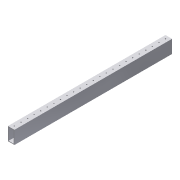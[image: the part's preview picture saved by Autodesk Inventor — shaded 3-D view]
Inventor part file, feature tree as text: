
AUTODESK INVENTOR PART (.ipt)
format: ipt  version: 2015 (Build 190159000, 159)  size: 127,488 bytes
history: native  units: in
note: dims shown in document units (in); Inventor stores cm internally (conversion verified against a paired STEP export)
features: sketch x2, extrude x1, hole x1, pattern_linear x1
ambient origin geometry x8: Origin, YZ Plane, XZ Plane, XY Plane, X Axis, Y Axis, Z Axis, Center Point
bodies: Solid1 (feature_tree)
feature tree (5):
  extrude  "Extrusion1"  Depth=2.0in
  hole  "Hole1"  [1 undecoded]
  pattern_linear  "Rectangular Pattern1"  Spacing1=0.5in  [1 undecoded]
  sketch  "Sketch1"  dims[d0=1.0in d1=2.0in]
  sketch  "Sketch2"  dims[d2=0.1in d4=0.0in d6=0.5in d7=0.164in d8=0.75in d9=0.375in d10=0.25in d11=0.5635in d12=1.0in d13=0.8108in d14=12.2047in d16=2.0in]
note: 2 required parameter values undecoded (feature->parameter linkage not recoverable at this tier; creation-order binding heuristic only, values carry confidence <= 0.55)
